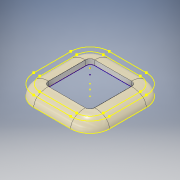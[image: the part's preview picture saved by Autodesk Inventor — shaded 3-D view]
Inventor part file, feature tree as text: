
AUTODESK INVENTOR PART (.ipt)
format: ipt  version: 2018.3 (Build 223284000, 284)  size: 345,600 bytes
history: native  units: in
note: dims shown in document units (in); Inventor stores cm internally (conversion verified against a paired STEP export)
features: other x8, extrude x2, projected_geometry x2
ambient origin geometry x8: Origin, YZ Plane, XZ Plane, XY Plane, X Axis, Y Axis, Z Axis, Center Point
bodies: Solid1 (feature_tree)
feature tree (12):
  other  "Case Top.ipt"
  extrude  "Inner Narrowing"  Depth=0.3937in
  extrude  "Opening Narrowing"  Depth=0.004in
  other  "Solid3::Case Top.ipt"
  other  "TaggingFeature1"
  other  "New peg sketch"
  other  "Alignment Sketch"
  other  "3/16" Vacuum Drill Sketch"
  other  "Inner Narrowing Sketch"
  projected_geometry  "Projected Loop1"
  other  "Opening Narrowing Sketch"
  projected_geometry  "Projected Loop2"
